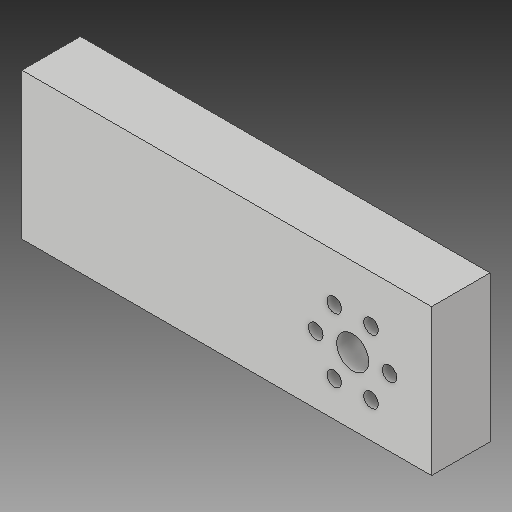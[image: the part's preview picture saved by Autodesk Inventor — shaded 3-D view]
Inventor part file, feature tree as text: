
AUTODESK INVENTOR PART (.ipt)
format: ipt  version: 2019 (Build 230136000, 136)  size: 140,288 bytes
history: native  units: in
note: dims shown in document units (in); Inventor stores cm internally (conversion verified against a paired STEP export)
features: thicken_offset x3, sketch x3, extrude x2, hole x1
ambient origin geometry x8: Origin, YZ Plane, XZ Plane, XY Plane, X Axis, Y Axis, Z Axis, Center Point
bodies: Solid1 (feature_tree)
feature tree (9):
  extrude  "Extrusion1"  Depth=1.25in
  extrude  "Extrusion2"  Depth=0.575in
  thicken_offset  "Thicken1"
  thicken_offset  "Thicken2"
  thicken_offset  "Thicken3"
  hole  "Hole1"  [1 undecoded]
  sketch  "Sketch1"  dims[d0=2.5in d1=1.25in]
  sketch  "Sketch2"  dims[d2=0.75in d3=0.0in d6=0.575in]
  sketch  "Sketch5"  dims[d7=0.275in d9=0.63in d15=0.75in d16=0.0in d17=0.125in d18=2.3622in d20=360.0deg d35=1.0in d36=1.0in d37=0.125in d38=0.125in d41=0.125in d42=0.125in d50=0.13in d51=0.25in d52=0.375in d53=0.25in d54=0.5635in d55=0.3in d56=0.8108in d57=0.25in d58=1.75in d59=3.5in d60=0.25in d61=0.674in]
note: 1 required parameter value undecoded (feature->parameter linkage not recoverable at this tier; creation-order binding heuristic only, values carry confidence <= 0.55)
